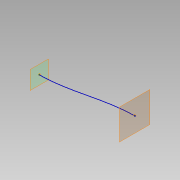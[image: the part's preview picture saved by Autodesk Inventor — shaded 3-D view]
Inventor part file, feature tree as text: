
AUTODESK INVENTOR PART (.ipt)
format: ipt  version: 2019 (Build 230136000, 136)  size: 87,552 bytes
history: native  units: mm
features: other x2, plane x2, sketch x1
ambient origin geometry x8: Origin, YZ Plane, XZ Plane, XY Plane, X Axis, Y Axis, Z Axis, Center Point
feature tree (5):
  other  "Punto de trabajo1"
  other  "Punto de trabajo2"
  plane  "Plano de trabajo1"
  plane  "Plano de trabajo2"
  sketch  "Boceto 3D1"  dims[d0=10.0mm d1=-0.1mm d2=10.0mm d3=-0.1mm]
